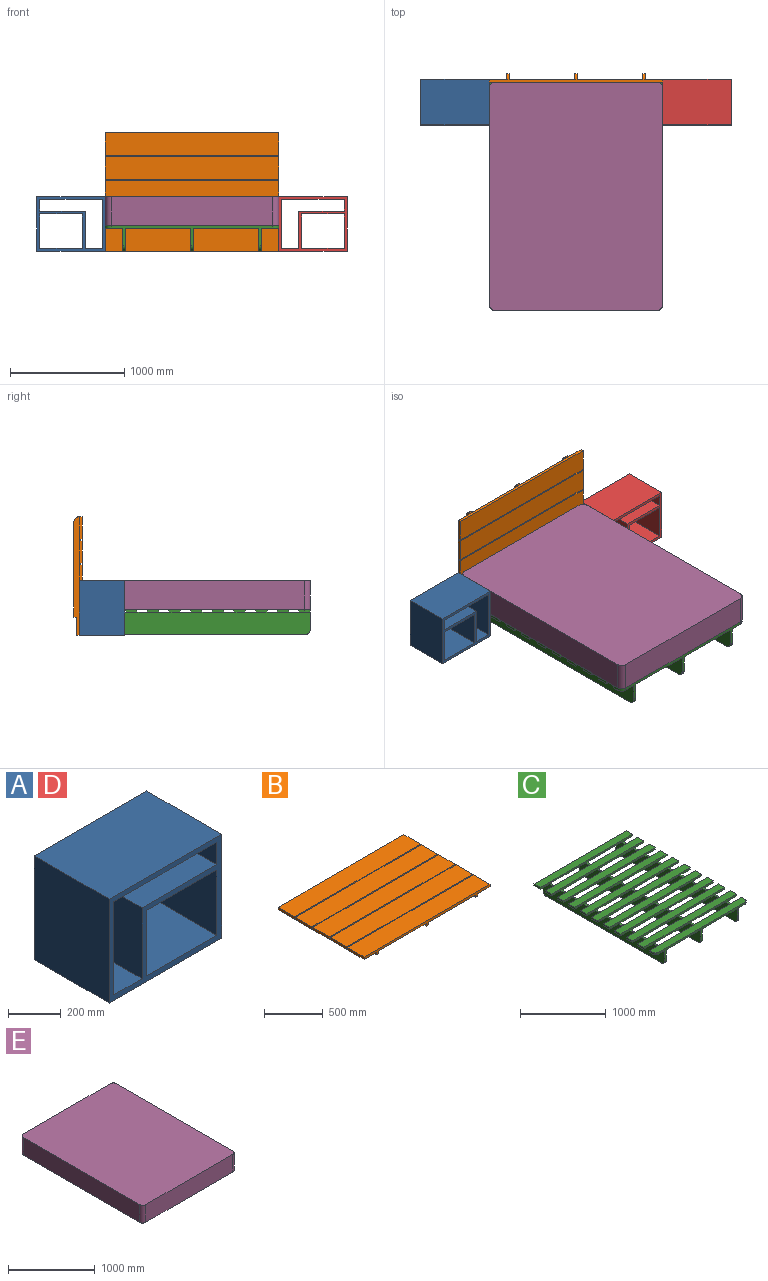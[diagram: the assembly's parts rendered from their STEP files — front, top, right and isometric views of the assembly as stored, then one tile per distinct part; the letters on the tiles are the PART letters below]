
ASSEMBLY  parts=5 mates=3
PART A: 16 faces, bbox 600x400x480 mm
  f0: plane 400x150mm, normal (0,0,1), area 60000mm2, adj f2,f10,f11,f14
  f1: plane 400x302.5mm, normal (-1,0,0), area 121000mm2, adj f2,f6,f11,f12
  f2: plane 600x480mm, normal (0,1,0), area 69062.5mm2, adj f0,f1,f3,f4,f5,f6,f7,f8
  f3: plane 600x400mm, normal (0,0,1), area 240000mm2, adj f2,f4,f9,f11
  f4: plane 480x400mm, normal (-1,0,0), area 192000mm2, adj f2,f3,f5,f11
  f5: plane 600x400mm, normal (0,0,-1), area 240000mm2, adj f2,f4,f9,f11
  f6: plane 400x375mm, normal (0,0,1), area 150000mm2, adj f1,f2,f11,f15
  f7: plane 550x400mm, normal (0,0,-1), area 220000mm2, adj f2,f8,f10,f11
  f8: plane 400x102.5mm, normal (-1,0,0), area 41000mm2, adj f2,f7,f11,f13
  f9: plane 480x400mm, normal (1,0,0), area 192000mm2, adj f2,f3,f5,f11
  f10: plane 430x400mm, normal (1,0,0), area 172000mm2, adj f0,f2,f7,f11
  f11: plane 600x480mm, normal (0,-1,0), area 69062.5mm2, adj f0,f1,f3,f4,f5,f6,f7,f8
  f12: plane 400x375mm, normal (0,0,-1), area 150000mm2, adj f1,f2,f11,f15
  f13: plane 400x400mm, normal (0,0,1), area 160000mm2, adj f2,f8,f11,f14
  f14: plane 400x327.5mm, normal (-1,0,0), area 131000mm2, adj f0,f2,f11,f13
  f15: plane 400x302.5mm, normal (1,0,0), area 121000mm2, adj f2,f6,f11,f12
PART B: 75 faces, bbox 1520x1040x75 mm
  f0: plane 1040x50mm, normal (1,0,0), area 47463.5mm2, adj f2,f15,f17,f27,f29,f38,f40,f49
  f1: plane 830x25mm, normal (0,0,-1), area 20750mm2, adj f6,f65,f66,f69
  f2: plane 1520x50mm, normal (0,-1,0), area 39875mm2, adj f0,f3,f4,f5,f6,f31,f32,f33
  f3: plane 1040x50mm, normal (-1,0,0), area 47463.5mm2, adj f2,f7,f16,f19,f28,f32,f39,f41
  f4: plane 1040x50mm, normal (1,0,0), area 47463.5mm2, adj f2,f8,f16,f20,f28,f33,f39,f42
  f5: plane 1040x50mm, normal (-1,0,0), area 47463.5mm2, adj f2,f8,f17,f20,f29,f33,f40,f42
  f6: plane 1040x50mm, normal (1,0,0), area 47463.5mm2, adj f1,f2,f7,f18,f19,f30,f32,f41
  f7: plane 572.5x200mm, normal (0,0,-1), area 114500mm2, adj f3,f6,f10,f12
  f8: plane 572.5x200mm, normal (0,0,-1), area 114500mm2, adj f4,f5,f10,f12
  f9: plane 200x150mm, normal (0,0,-1), area 30000mm2, adj f10,f12,f13,f65
  f10: plane 1520x25mm, normal (0,-1,0), area 38000mm2, adj f7,f8,f9,f11,f13,f14,f15,f18
  f11: plane 200x25mm, normal (1,0,0), area 5000mm2, adj f10,f12,f14,f15
  f12: plane 1520x25mm, normal (0,1,0), area 38000mm2, adj f7,f8,f9,f11,f13,f14,f15,f16
  f13: plane 200x25mm, normal (-1,0,0), area 5000mm2, adj f9,f10,f12,f14
  f14: plane 1520x200mm, normal (0,0,1), area 304000mm2, adj f10,f11,f12,f13
  f15: plane 200x150mm, normal (0,0,-1), area 30000mm2, adj f0,f10,f11,f12
  f16: plane 25x10mm, normal (0,0,1), area 250mm2, adj f3,f4,f12,f44
  f17: plane 25x10mm, normal (0,0,1), area 250mm2, adj f0,f5,f12,f44
  f18: plane 25x10mm, normal (0,0,1), area 250mm2, adj f6,f10,f23,f65
  f19: plane 572.5x200mm, normal (0,0,-1), area 114500mm2, adj f3,f6,f23,f25
  f20: plane 572.5x200mm, normal (0,0,-1), area 114500mm2, adj f4,f5,f23,f25
  f21: plane 200x150mm, normal (0,0,-1), area 30000mm2, adj f23,f24,f25,f65
  f22: plane 200x25mm, normal (1,0,0), area 5000mm2, adj f23,f25,f26,f27
  f23: plane 1520x25mm, normal (0,1,0), area 38000mm2, adj f18,f19,f20,f21,f22,f24,f26,f27
  f24: plane 200x25mm, normal (-1,0,0), area 5000mm2, adj f21,f23,f25,f26
  f25: plane 1520x25mm, normal (0,-1,0), area 38000mm2, adj f19,f20,f21,f22,f24,f26,f27,f30
  f26: plane 1520x200mm, normal (0,0,1), area 304000mm2, adj f22,f23,f24,f25
  f27: plane 200x150mm, normal (0,0,-1), area 30000mm2, adj f0,f22,f23,f25
  f28: plane 25x10mm, normal (0,0,1), area 250mm2, adj f3,f4,f10,f23
  f29: plane 25x10mm, normal (0,0,1), area 250mm2, adj f0,f5,f10,f23
  f30: plane 25x10mm, normal (0,0,1), area 250mm2, adj f6,f25,f35,f65
  f31: plane 200x150mm, normal (0,0,-1), area 30000mm2, adj f2,f35,f36,f65
  f32: plane 572.5x200mm, normal (0,0,-1), area 114500mm2, adj f2,f3,f6,f35
  f33: plane 572.5x200mm, normal (0,0,-1), area 114500mm2, adj f2,f4,f5,f35
  f34: plane 200x25mm, normal (1,0,0), area 5000mm2, adj f2,f35,f37,f38
  f35: plane 1520x25mm, normal (0,1,0), area 38000mm2, adj f30,f31,f32,f33,f34,f36,f37,f38
  f36: plane 200x25mm, normal (-1,0,0), area 5000mm2, adj f2,f31,f35,f37
  f37: plane 1520x200mm, normal (0,0,1), area 304000mm2, adj f2,f34,f35,f36
  f38: plane 200x150mm, normal (0,0,-1), area 30000mm2, adj f0,f2,f34,f35
  f39: plane 25x10mm, normal (0,0,1), area 250mm2, adj f3,f4,f25,f35
  f40: plane 25x10mm, normal (0,0,1), area 250mm2, adj f0,f5,f25,f35
  f41: plane 572.5x200mm, normal (0,0,-1), area 114500mm2, adj f3,f6,f44,f46
  f42: plane 572.5x200mm, normal (0,0,-1), area 114500mm2, adj f4,f5,f44,f46
  f43: plane 200x150mm, normal (0,0,-1), area 30000mm2, adj f44,f46,f47,f65
  f44: plane 1520x25mm, normal (0,-1,0), area 38000mm2, adj f16,f17,f41,f42,f43,f45,f47,f48
  f45: plane 200x25mm, normal (1,0,0), area 5000mm2, adj f44,f46,f48,f49
  f46: plane 1520x25mm, normal (0,1,0), area 38000mm2, adj f41,f42,f43,f45,f47,f48,f49,f50
  f47: plane 200x25mm, normal (-1,0,0), area 5000mm2, adj f43,f44,f46,f48
  f48: plane 1520x200mm, normal (0,0,1), area 304000mm2, adj f44,f45,f46,f47
  f49: plane 200x150mm, normal (0,0,-1), area 30000mm2, adj f0,f44,f45,f46
  f50: plane 25x10mm, normal (0,0,1), area 250mm2, adj f3,f4,f46,f56
  f51: plane 25x10mm, normal (0,0,1), area 250mm2, adj f0,f5,f46,f56
  f52: plane 25x10mm, normal (0,0,1), area 250mm2, adj f6,f12,f44,f65
  f53: plane 200x150mm, normal (0,0,-1), area 30000mm2, adj f56,f58,f59,f65
  f54: plane 572.5x200mm, normal (0,0,-1), area 114500mm2, adj f4,f5,f56,f58
  f55: plane 572.5x200mm, normal (0,0,-1), area 114500mm2, adj f3,f6,f56,f58
  f56: plane 1520x25mm, normal (0,-1,0), area 38000mm2, adj f50,f51,f53,f54,f55,f57,f59,f60
  f57: plane 200x25mm, normal (1,0,0), area 5000mm2, adj f56,f58,f60,f61
  f58: plane 1520x25mm, normal (0,1,0), area 38000mm2, adj f53,f54,f55,f57,f59,f60,f61,f66
  f59: plane 200x25mm, normal (-1,0,0), area 5000mm2, adj f53,f56,f58,f60
  f60: plane 1520x200mm, normal (0,0,1), area 304000mm2, adj f56,f57,f58,f59
  f61: plane 200x150mm, normal (0,0,-1), area 30000mm2, adj f0,f56,f57,f58
  f62: plane 830x25mm, normal (0,0,-1), area 20750mm2, adj f3,f4,f67,f74
  f63: plane 830x25mm, normal (0,0,-1), area 20750mm2, adj f0,f5,f68,f71
  f64: plane 25x10mm, normal (0,0,1), area 250mm2, adj f6,f46,f56,f65
  f65: plane 1040x50mm, normal (-1,0,0), area 47463.5mm2, adj f1,f2,f9,f18,f21,f30,f31,f43
  f66: cylinder r=50mm len=50mm, axis (1,0,0), area 1963.5mm2, adj f1,f6,f58,f65
  f67: cylinder r=50mm len=50mm, axis (1,0,0), area 1963.5mm2, adj f3,f4,f58,f62
  f68: cylinder r=50mm len=50mm, axis (1,0,0), area 1963.5mm2, adj f0,f5,f58,f63
  f69: plane 25x25mm, normal (0,-1,0), area 625mm2, adj f1,f6,f65,f70
  f70: plane 160x25mm, normal (0,0,-1), area 4000mm2, adj f2,f6,f65,f69
  f71: plane 25x25mm, normal (0,-1,0), area 625mm2, adj f0,f5,f63,f72
  f72: plane 160x25mm, normal (0,0,-1), area 4000mm2, adj f0,f2,f5,f71
  f73: plane 160x25mm, normal (0,0,-1), area 4000mm2, adj f2,f3,f4,f74
  f74: plane 25x25mm, normal (0,-1,0), area 625mm2, adj f3,f4,f62,f73
PART C: 146 faces, bbox 1520x2000x225 mm
  f0: plane 90x25mm, normal (0,0,1), area 2250mm2, adj f37,f39,f54,f88
  f1: plane 90x25mm, normal (0,0,1), area 2250mm2, adj f37,f39,f72,f79
  f2: plane 90x25mm, normal (0,0,1), area 2250mm2, adj f32,f37,f39,f70
  f3: plane 90x25mm, normal (0,0,1), area 2250mm2, adj f37,f39,f64,f90
  f4: plane 90x25mm, normal (0,0,1), area 2250mm2, adj f37,f39,f56,f81
  f5: plane 90x25mm, normal (0,0,1), area 2250mm2, adj f37,f39,f124,f135
  f6: plane 90x25mm, normal (0,0,1), area 2250mm2, adj f37,f39,f116,f126
  f7: plane 90x25mm, normal (0,0,1), area 2250mm2, adj f37,f39,f106,f114
  f8: plane 90x25mm, normal (0,0,1), area 2250mm2, adj f37,f39,f98,f108
  f9: plane 90x25mm, normal (0,0,1), area 2250mm2, adj f40,f42,f54,f88
  f10: plane 90x25mm, normal (0,0,1), area 2250mm2, adj f40,f42,f72,f79
  f11: plane 90x25mm, normal (0,0,1), area 2250mm2, adj f32,f40,f42,f70
  f12: plane 90x25mm, normal (0,0,1), area 2250mm2, adj f40,f42,f64,f90
  f13: plane 90x25mm, normal (0,0,1), area 2250mm2, adj f40,f42,f56,f81
  f14: plane 90x25mm, normal (0,0,1), area 2250mm2, adj f40,f42,f124,f135
  f15: plane 90x25mm, normal (0,0,1), area 2250mm2, adj f40,f42,f116,f126
  f16: plane 90x25mm, normal (0,0,1), area 2250mm2, adj f40,f42,f106,f114
  f17: plane 90x25mm, normal (0,0,1), area 2250mm2, adj f40,f42,f98,f108
  f18: plane 90x25mm, normal (0,0,1), area 2250mm2, adj f30,f45,f47,f133
  f19: plane 90x25mm, normal (0,0,1), area 2250mm2, adj f45,f47,f124,f135
  f20: plane 90x25mm, normal (0,0,1), area 2250mm2, adj f45,f47,f116,f126
  f21: plane 90x25mm, normal (0,0,1), area 2250mm2, adj f45,f47,f106,f114
  f22: plane 90x25mm, normal (0,0,1), area 2250mm2, adj f45,f47,f98,f108
  f23: plane 90x25mm, normal (0,0,1), area 2250mm2, adj f45,f47,f64,f90
  f24: plane 90x25mm, normal (0,0,1), area 2250mm2, adj f45,f47,f56,f81
  f25: plane 90x25mm, normal (0,0,1), area 2250mm2, adj f45,f47,f72,f79
  f26: plane 90x25mm, normal (0,0,1), area 2250mm2, adj f45,f47,f54,f88
  f27: plane 150x100mm, normal (0,0,-1), area 15000mm2, adj f30,f32,f33,f45
  f28: plane 572.5x100mm, normal (0,0,-1), area 57250mm2, adj f30,f32,f39,f42
  f29: plane 572.5x100mm, normal (0,0,-1), area 57250mm2, adj f30,f32,f37,f47
  f30: plane 1520x25mm, normal (0,-1,0), area 38000mm2, adj f18,f27,f28,f29,f31,f33,f34,f35
  f31: plane 100x25mm, normal (1,0,0), area 2500mm2, adj f30,f32,f34,f35
  f32: plane 1520x25mm, normal (0,1,0), area 38000mm2, adj f2,f11,f27,f28,f29,f31,f33,f34
  f33: plane 100x25mm, normal (-1,0,0), area 2500mm2, adj f27,f30,f32,f34
  f34: plane 1520x100mm, normal (0,0,1), area 152000mm2, adj f30,f31,f32,f33
  f35: plane 150x100mm, normal (0,0,-1), area 15000mm2, adj f30,f31,f32,f40
  f36: plane 90x25mm, normal (0,0,1), area 2250mm2, adj f30,f37,f39,f133
  f37: plane 2000x200mm, normal (-1,0,0), area 398927mm2, adj f0,f1,f2,f3,f4,f5,f6,f7
  f38: plane 1900x25mm, normal (0,0,-1), area 47500mm2, adj f37,f39,f139,f142
  f39: plane 2000x200mm, normal (1,0,0), area 398927mm2, adj f0,f1,f2,f3,f4,f5,f6,f7
  f40: plane 2000x200mm, normal (1,0,0), area 398927mm2, adj f9,f10,f11,f12,f13,f14,f15,f16
  f41: plane 90x25mm, normal (0,0,1), area 2250mm2, adj f30,f40,f42,f133
  f42: plane 2000x200mm, normal (-1,0,0), area 398927mm2, adj f9,f10,f11,f12,f13,f14,f15,f16
  f43: plane 1900x25mm, normal (0,0,-1), area 47500mm2, adj f40,f42,f140,f143
  f44: plane 90x25mm, normal (0,0,1), area 2250mm2, adj f32,f45,f47,f70
  f45: plane 2000x200mm, normal (-1,0,0), area 398927mm2, adj f18,f19,f20,f21,f22,f23,f24,f25
  f46: plane 1900x25mm, normal (0,0,-1), area 47500mm2, adj f45,f47,f138,f141
  f47: plane 2000x200mm, normal (1,0,0), area 398927mm2, adj f18,f19,f20,f21,f22,f23,f24,f25
  f48: plane 1420x175mm, normal (0,-1,0), area 46750mm2, adj f37,f39,f40,f42,f45,f47,f94,f95
  f49: plane 1520x175mm, normal (0,1,0), area 49250mm2, adj f37,f39,f40,f42,f45,f47,f59,f60
  f50: plane 572.5x100mm, normal (0,0,-1), area 57250mm2, adj f39,f42,f54,f56
  f51: plane 150x100mm, normal (0,0,-1), area 15000mm2, adj f40,f53,f54,f56
  f52: plane 572.5x100mm, normal (0,0,-1), area 57250mm2, adj f37,f47,f54,f56
  f53: plane 100x25mm, normal (1,0,0), area 2500mm2, adj f51,f54,f56,f57
  f54: plane 1520x25mm, normal (0,1,0), area 38000mm2, adj f0,f9,f26,f50,f51,f52,f53,f55
  f55: plane 100x25mm, normal (-1,0,0), area 2500mm2, adj f54,f56,f57,f58
  f56: plane 1520x25mm, normal (0,-1,0), area 38000mm2, adj f4,f13,f24,f50,f51,f52,f53,f55
  f57: plane 1520x100mm, normal (0,0,1), area 152000mm2, adj f53,f54,f55,f56
  f58: plane 150x100mm, normal (0,0,-1), area 15000mm2, adj f45,f54,f55,f56
  f59: plane 572.5x100mm, normal (0,0,-1), area 57250mm2, adj f39,f42,f49,f64
  f60: plane 150x100mm, normal (0,0,-1), area 15000mm2, adj f40,f49,f62,f64
  f61: plane 572.5x100mm, normal (0,0,-1), area 57250mm2, adj f37,f47,f49,f64
  f62: plane 100x25mm, normal (1,0,0), area 2500mm2, adj f49,f60,f64,f65
  f63: plane 100x25mm, normal (-1,0,0), area 2500mm2, adj f49,f64,f65,f66
  f64: plane 1520x25mm, normal (0,-1,0), area 38000mm2, adj f3,f12,f23,f59,f60,f61,f62,f63
  f65: plane 1520x100mm, normal (0,0,1), area 152000mm2, adj f49,f62,f63,f64
  f66: plane 150x100mm, normal (0,0,-1), area 15000mm2, adj f45,f49,f63,f64
  f67: plane 572.5x100mm, normal (0,0,-1), area 57250mm2, adj f39,f42,f70,f72
  f68: plane 150x100mm, normal (0,0,-1), area 15000mm2, adj f40,f70,f71,f72
  f69: plane 572.5x100mm, normal (0,0,-1), area 57250mm2, adj f37,f47,f70,f72
  f70: plane 1520x25mm, normal (0,-1,0), area 38000mm2, adj f2,f11,f44,f67,f68,f69,f71,f73
  f71: plane 100x25mm, normal (1,0,0), area 2500mm2, adj f68,f70,f72,f74
  f72: plane 1520x25mm, normal (0,1,0), area 38000mm2, adj f1,f10,f25,f67,f68,f69,f71,f73
  f73: plane 100x25mm, normal (-1,0,0), area 2500mm2, adj f70,f72,f74,f75
  f74: plane 1520x100mm, normal (0,0,1), area 152000mm2, adj f70,f71,f72,f73
  f75: plane 150x100mm, normal (0,0,-1), area 15000mm2, adj f45,f70,f72,f73
  f76: plane 572.5x100mm, normal (0,0,-1), area 57250mm2, adj f39,f42,f79,f81
  f77: plane 150x100mm, normal (0,0,-1), area 15000mm2, adj f40,f79,f80,f81
  f78: plane 572.5x100mm, normal (0,0,-1), area 57250mm2, adj f37,f47,f79,f81
  f79: plane 1520x25mm, normal (0,-1,0), area 38000mm2, adj f1,f10,f25,f76,f77,f78,f80,f82
  f80: plane 100x25mm, normal (1,0,0), area 2500mm2, adj f77,f79,f81,f83
  f81: plane 1520x25mm, normal (0,1,0), area 38000mm2, adj f4,f13,f24,f76,f77,f78,f80,f82
  f82: plane 100x25mm, normal (-1,0,0), area 2500mm2, adj f79,f81,f83,f84
  f83: plane 1520x100mm, normal (0,0,1), area 152000mm2, adj f79,f80,f81,f82
  f84: plane 150x100mm, normal (0,0,-1), area 15000mm2, adj f45,f79,f81,f82
  f85: plane 572.5x100mm, normal (0,0,-1), area 57250mm2, adj f39,f42,f88,f90
  f86: plane 150x100mm, normal (0,0,-1), area 15000mm2, adj f40,f88,f89,f90
  f87: plane 572.5x100mm, normal (0,0,-1), area 57250mm2, adj f37,f47,f88,f90
  f88: plane 1520x25mm, normal (0,-1,0), area 38000mm2, adj f0,f9,f26,f85,f86,f87,f89,f91
  f89: plane 100x25mm, normal (1,0,0), area 2500mm2, adj f86,f88,f90,f92
  f90: plane 1520x25mm, normal (0,1,0), area 38000mm2, adj f3,f12,f23,f85,f86,f87,f89,f91
  f91: plane 100x25mm, normal (-1,0,0), area 2500mm2, adj f88,f90,f92,f93
  f92: plane 1520x100mm, normal (0,0,1), area 152000mm2, adj f88,f89,f90,f91
  f93: plane 150x100mm, normal (0,0,-1), area 15000mm2, adj f45,f88,f90,f91
  f94: plane 572.5x100mm, normal (0,0,-1), area 57250mm2, adj f39,f42,f48,f98
  f95: plane 150x100mm, normal (0,0,-1), area 14463.5mm2, adj f40,f48,f97,f98,f145
  f96: plane 572.5x100mm, normal (0,0,-1), area 57250mm2, adj f37,f47,f48,f98
  f97: plane 50x25mm, normal (1,0,0), area 1250mm2, adj f95,f98,f100,f145
  f98: plane 1520x25mm, normal (0,1,0), area 38000mm2, adj f8,f17,f22,f94,f95,f96,f97,f99
  f99: plane 50x25mm, normal (-1,0,0), area 1250mm2, adj f98,f100,f101,f144
  f100: plane 1520x100mm, normal (0,0,1), area 150927mm2, adj f48,f97,f98,f99,f144,f145
  f101: plane 150x100mm, normal (0,0,-1), area 14463.5mm2, adj f45,f48,f98,f99,f144
  f102: plane 572.5x100mm, normal (0,0,-1), area 57250mm2, adj f39,f42,f106,f108
  f103: plane 150x100mm, normal (0,0,-1), area 15000mm2, adj f40,f105,f106,f108
  f104: plane 572.5x100mm, normal (0,0,-1), area 57250mm2, adj f37,f47,f106,f108
  f105: plane 100x25mm, normal (1,0,0), area 2500mm2, adj f103,f106,f108,f109
  f106: plane 1520x25mm, normal (0,1,0), area 38000mm2, adj f7,f16,f21,f102,f103,f104,f105,f107
  f107: plane 100x25mm, normal (-1,0,0), area 2500mm2, adj f106,f108,f109,f110
  f108: plane 1520x25mm, normal (0,-1,0), area 38000mm2, adj f8,f17,f22,f102,f103,f104,f105,f107
  f109: plane 1520x100mm, normal (0,0,1), area 152000mm2, adj f105,f106,f107,f108
  f110: plane 150x100mm, normal (0,0,-1), area 15000mm2, adj f45,f106,f107,f108
  f111: plane 572.5x100mm, normal (0,0,-1), area 57250mm2, adj f39,f42,f114,f116
  f112: plane 150x100mm, normal (0,0,-1), area 15000mm2, adj f40,f114,f115,f116
  f113: plane 572.5x100mm, normal (0,0,-1), area 57250mm2, adj f37,f47,f114,f116
  f114: plane 1520x25mm, normal (0,-1,0), area 38000mm2, adj f7,f16,f21,f111,f112,f113,f115,f117
  f115: plane 100x25mm, normal (1,0,0), area 2500mm2, adj f112,f114,f116,f118
  f116: plane 1520x25mm, normal (0,1,0), area 38000mm2, adj f6,f15,f20,f111,f112,f113,f115,f117
  f117: plane 100x25mm, normal (-1,0,0), area 2500mm2, adj f114,f116,f118,f119
  f118: plane 1520x100mm, normal (0,0,1), area 152000mm2, adj f114,f115,f116,f117
  f119: plane 150x100mm, normal (0,0,-1), area 15000mm2, adj f45,f114,f116,f117
  f120: plane 572.5x100mm, normal (0,0,-1), area 57250mm2, adj f39,f42,f124,f126
  f121: plane 150x100mm, normal (0,0,-1), area 15000mm2, adj f40,f123,f124,f126
  f122: plane 572.5x100mm, normal (0,0,-1), area 57250mm2, adj f37,f47,f124,f126
  f123: plane 100x25mm, normal (1,0,0), area 2500mm2, adj f121,f124,f126,f127
  f124: plane 1520x25mm, normal (0,1,0), area 38000mm2, adj f5,f14,f19,f120,f121,f122,f123,f125
  f125: plane 100x25mm, normal (-1,0,0), area 2500mm2, adj f124,f126,f127,f128
  f126: plane 1520x25mm, normal (0,-1,0), area 38000mm2, adj f6,f15,f20,f120,f121,f122,f123,f125
  f127: plane 1520x100mm, normal (0,0,1), area 152000mm2, adj f123,f124,f125,f126
  f128: plane 150x100mm, normal (0,0,-1), area 15000mm2, adj f45,f124,f125,f126
  f129: plane 572.5x100mm, normal (0,0,-1), area 57250mm2, adj f39,f42,f133,f135
  f130: plane 150x100mm, normal (0,0,-1), area 15000mm2, adj f40,f132,f133,f135
  f131: plane 572.5x100mm, normal (0,0,-1), area 57250mm2, adj f37,f47,f133,f135
  f132: plane 100x25mm, normal (1,0,0), area 2500mm2, adj f130,f133,f135,f136
  f133: plane 1520x25mm, normal (0,1,0), area 38000mm2, adj f18,f36,f41,f129,f130,f131,f132,f134
  f134: plane 100x25mm, normal (-1,0,0), area 2500mm2, adj f133,f135,f136,f137
  f135: plane 1520x25mm, normal (0,-1,0), area 38000mm2, adj f5,f14,f19,f129,f130,f131,f132,f134
  f136: plane 1520x100mm, normal (0,0,1), area 152000mm2, adj f132,f133,f134,f135
  f137: plane 150x100mm, normal (0,0,-1), area 15000mm2, adj f45,f133,f134,f135
  f138: cylinder r=50mm len=50mm, axis (-1,0,0), area 1963.5mm2, adj f45,f46,f47,f48
  f139: cylinder r=50mm len=50mm, axis (-1,0,0), area 1963.5mm2, adj f37,f38,f39,f48
  f140: cylinder r=50mm len=50mm, axis (-1,0,0), area 1963.5mm2, adj f40,f42,f43,f48
  f141: cylinder r=50mm len=50mm, axis (1,0,0), area 1963.5mm2, adj f45,f46,f47,f49
  f142: cylinder r=50mm len=50mm, axis (1,0,0), area 1963.5mm2, adj f37,f38,f39,f49
  f143: cylinder r=50mm len=50mm, axis (1,0,0), area 1963.5mm2, adj f40,f42,f43,f49
  f144: cylinder r=50mm len=50mm, axis (0,0,1), area 1963.5mm2, adj f48,f99,f100,f101
  f145: cylinder r=50mm len=50mm, axis (0,0,-1), area 1963.5mm2, adj f48,f95,f97,f100
PART D: same geometry as A
PART E: 10 faces, bbox 1520x2000x250 mm
  f0: plane 1420x250mm, normal (0,1,0), area 355000mm2, adj f1,f7,f8,f9
  f1: cylinder r=50mm len=250mm, axis (0,0,-1), area 19635mm2, adj f0,f2,f8,f9
  f2: plane 1900x250mm, normal (-1,0,0), area 475000mm2, adj f1,f3,f8,f9
  f3: cylinder r=50mm len=250mm, axis (0,0,-1), area 19635mm2, adj f2,f4,f8,f9
  f4: plane 1420x250mm, normal (0,-1,0), area 355000mm2, adj f3,f5,f8,f9
  f5: cylinder r=50mm len=250mm, axis (0,0,-1), area 19635mm2, adj f4,f6,f8,f9
  f6: plane 1900x250mm, normal (1,0,0), area 475000mm2, adj f5,f7,f8,f9
  f7: cylinder r=50mm len=250mm, axis (0,0,-1), area 19635mm2, adj f0,f6,f8,f9
  f8: plane 2000x1520mm, normal (0,0,1), area 3037854mm2, adj f0,f1,f2,f3,f4,f5,f6,f7
  f9: plane 2000x1520mm, normal (0,0,-1), area 3037854mm2, adj f0,f1,f2,f3,f4,f5,f6,f7
PLACE A rot(axis=(0,0,1),180deg) t=(-760,625,-203.49)mm
PLACE B rot(axis=(1,0,0),90deg) t=(0,1025,316.51)mm
PLACE C at identity fixed
PLACE D t=(760,1025,-203.49)mm
PLACE E t=(0,0,25)mm
MATE fastened A.f5 <-> B.f2  axis (0,0,1) through (-760,1025,-203.49)mm
MATE parallel B.f37 <-> C.f49  axis (0,-1,0) through (0,1000,-103.49)mm
MATE fastened B.f38 <-> D.f2  axis (0,-1,0) through (760,1025,-203.49)mm
